# Revit family: Nawiewnik wirowy NWO-11
name_source: partatom
category: Terminale wentylacyjne
revit_build: Autodesk Revit 2018 (Build: 20190510_1515(x64)
units: mm (PartAtom-declared; Revit-internal decimal feet)

## family parameters
Numer OmniClass = 23.75.70.21.27.11
Oparty na płaszczyźnie roboczej = Nie
Punkt obliczania pomieszczeń = Nie
Tnij formami wycięć po wczytaniu = Nie
Typ części = Normalny
Tytuł OmniClass = Diffusers, Registers, and Grilles
Współdzielony = Nie
Wymiar okrągłego złącza = Użyj średnicy
Zawsze pionowo = Tak

## types (27) — shared parameters
Atest Higieniczny = HK/K/0522/01/2016
Deklaracja zgodności = 1/DZ/2020/K
IfcExportAs = IfcFlowTerminal
Karta katalogowa = https://www.sawpol.pl
Komentarze do typu = Nawiewnik wirowy
Model = NWO-11
Obraz typu = NWO-11.PNG
Producent = PPHU SAW-POL
URL = https://www.sawpol.pl
Wysokość = 160 mm  [stored 0.524934 ft]

## per-type parameters (varying)
| type | Materiał | Materiał piór | Promień wewnętrzny | Promień zewnętrzny | Wielkość | Wykonanie aluminium | Wykonanie stal lakierowana | Wykonanie stal nierdzewna | Średnica wewnętrzna | Średnica zewnętrzna |
| 250 ST | SAW-POL Stal lakierowana | SAW-POL Stal lakierowana | 123 mm | 153 mm | 250 mm  [stored 0.82021 ft] | Nie | Tak | Nie | 245 mm  [stored 0.803806 ft] | 305 mm  [stored 1.00066 ft] |
| 315 ST | SAW-POL Stal lakierowana | SAW-POL Stal lakierowana | 155 mm  [stored 0.50853 ft] | 185 mm  [stored 0.606955 ft] | 315 mm  [stored 1.03346 ft] | Nie | Tak | Nie | 310 mm  [stored 1.01706 ft] | 370 mm  [stored 1.21391 ft] |
| 355 ST | SAW-POL Stal lakierowana | SAW-POL Stal lakierowana | 175 mm  [stored 0.574147 ft] | 205 mm  [stored 0.672572 ft] | 355 mm | Nie | Tak | Nie | 350 mm  [stored 1.14829 ft] | 410 mm  [stored 1.34514 ft] |
| 400 ST | SAW-POL Stal lakierowana | SAW-POL Stal lakierowana | 198 mm | 238 mm | 400 mm  [stored 1.31234 ft] | Nie | Tak | Nie | 395 mm  [stored 1.29593 ft] | 475 mm  [stored 1.5584 ft] |
| 500 ST | SAW-POL Stal lakierowana | SAW-POL Stal lakierowana | 248 mm  [stored 0.813648 ft] | 298 mm | 500 mm  [stored 1.64042 ft] | Nie | Tak | Nie | 495 mm  [stored 1.62402 ft] | 595 mm  [stored 1.9521 ft] |
| 630 ST | SAW-POL Stal lakierowana | SAW-POL Stal lakierowana | 313 mm | 373 mm | 630 mm  [stored 2.06693 ft] | Nie | Tak | Nie | 625 mm  [stored 2.05052 ft] | 745 mm  [stored 2.44423 ft] |
| 710 ST | SAW-POL Stal lakierowana | SAW-POL Stal lakierowana | 353 mm | 423 mm | 710 mm | Nie | Tak | Nie | 705 mm  [stored 2.31299 ft] | 845 mm |
| 800 ST | SAW-POL Stal lakierowana | SAW-POL Stal lakierowana | 398 mm | 468 mm | 800 mm | Nie | Tak | Nie | 795 mm  [stored 2.60827 ft] | 935 mm |
| 1000 ST | SAW-POL Stal lakierowana | SAW-POL Stal lakierowana | 498 mm | 588 mm | 1000 mm | Nie | Tak | Nie | 995 mm | 1175 mm |
| 250 AL | SAW-POL Aluminium | SAW-POL Aluminium | 123 mm | 153 mm | 250 mm  [stored 0.82021 ft] | Tak | Nie | Nie | 245 mm  [stored 0.803806 ft] | 305 mm  [stored 1.00066 ft] |
| 315 AL | SAW-POL Aluminium | SAW-POL Aluminium | 155 mm  [stored 0.50853 ft] | 185 mm  [stored 0.606955 ft] | 315 mm  [stored 1.03346 ft] | Tak | Nie | Nie | 310 mm  [stored 1.01706 ft] | 370 mm  [stored 1.21391 ft] |
| 355 AL | SAW-POL Aluminium | SAW-POL Aluminium | 175 mm  [stored 0.574147 ft] | 205 mm  [stored 0.672572 ft] | 355 mm | Tak | Nie | Nie | 350 mm  [stored 1.14829 ft] | 410 mm  [stored 1.34514 ft] |
| 400 AL | SAW-POL Aluminium | SAW-POL Aluminium | 198 mm | 238 mm | 400 mm  [stored 1.31234 ft] | Tak | Nie | Nie | 395 mm  [stored 1.29593 ft] | 475 mm  [stored 1.5584 ft] |
| 500 AL | SAW-POL Aluminium | SAW-POL Aluminium | 248 mm  [stored 0.813648 ft] | 298 mm | 500 mm  [stored 1.64042 ft] | Tak | Nie | Nie | 495 mm  [stored 1.62402 ft] | 595 mm  [stored 1.9521 ft] |
| 630 AL | SAW-POL Aluminium | SAW-POL Aluminium | 313 mm | 373 mm | 630 mm  [stored 2.06693 ft] | Tak | Nie | Nie | 625 mm  [stored 2.05052 ft] | 745 mm  [stored 2.44423 ft] |
| 710 AL | SAW-POL Aluminium | SAW-POL Aluminium | 353 mm | 423 mm | 710 mm | Tak | Nie | Nie | 705 mm  [stored 2.31299 ft] | 845 mm |
| 800 AL | SAW-POL Aluminium | SAW-POL Aluminium | 398 mm | 468 mm | 800 mm | Tak | Nie | Nie | 795 mm  [stored 2.60827 ft] | 935 mm |
| 1000 AL | SAW-POL Aluminium | SAW-POL Aluminium | 498 mm | 588 mm | 1000 mm | Tak | Nie | Nie | 995 mm | 1175 mm |
| 250 KO | SAW-POL Stal nierdzewna | SAW-POL Stal nierdzewna | 123 mm | 153 mm | 250 mm  [stored 0.82021 ft] | Nie | Nie | Tak | 245 mm  [stored 0.803806 ft] | 305 mm  [stored 1.00066 ft] |
| 315 KO | SAW-POL Stal nierdzewna | SAW-POL Stal nierdzewna | 155 mm  [stored 0.50853 ft] | 185 mm  [stored 0.606955 ft] | 315 mm  [stored 1.03346 ft] | Nie | Nie | Tak | 310 mm  [stored 1.01706 ft] | 370 mm  [stored 1.21391 ft] |
| 355 KO | SAW-POL Stal nierdzewna | SAW-POL Stal nierdzewna | 175 mm  [stored 0.574147 ft] | 205 mm  [stored 0.672572 ft] | 355 mm | Nie | Nie | Tak | 350 mm  [stored 1.14829 ft] | 410 mm  [stored 1.34514 ft] |
| 400 KO | SAW-POL Stal nierdzewna | SAW-POL Stal nierdzewna | 198 mm | 238 mm | 400 mm  [stored 1.31234 ft] | Nie | Nie | Tak | 395 mm  [stored 1.29593 ft] | 475 mm  [stored 1.5584 ft] |
| 500 KO | SAW-POL Stal nierdzewna | SAW-POL Stal nierdzewna | 248 mm  [stored 0.813648 ft] | 298 mm | 500 mm  [stored 1.64042 ft] | Nie | Nie | Tak | 495 mm  [stored 1.62402 ft] | 595 mm  [stored 1.9521 ft] |
| 630 KO | SAW-POL Stal nierdzewna | SAW-POL Stal nierdzewna | 313 mm | 373 mm | 630 mm  [stored 2.06693 ft] | Nie | Nie | Tak | 625 mm  [stored 2.05052 ft] | 745 mm  [stored 2.44423 ft] |
| 710 KO | SAW-POL Stal nierdzewna | SAW-POL Stal nierdzewna | 353 mm | 423 mm | 710 mm | Nie | Nie | Tak | 705 mm  [stored 2.31299 ft] | 845 mm |
| 800 KO | SAW-POL Stal nierdzewna | SAW-POL Stal nierdzewna | 398 mm | 468 mm | 800 mm | Nie | Nie | Tak | 795 mm  [stored 2.60827 ft] | 935 mm |
| 1000 KO | SAW-POL Stal nierdzewna | SAW-POL Stal nierdzewna | 498 mm | 588 mm | 1000 mm | Nie | Nie | Tak | 995 mm | 1175 mm |

note: [stored X ft] marks values corroborated as IEEE doubles in the binary element streams (Revit-internal decimal feet)
